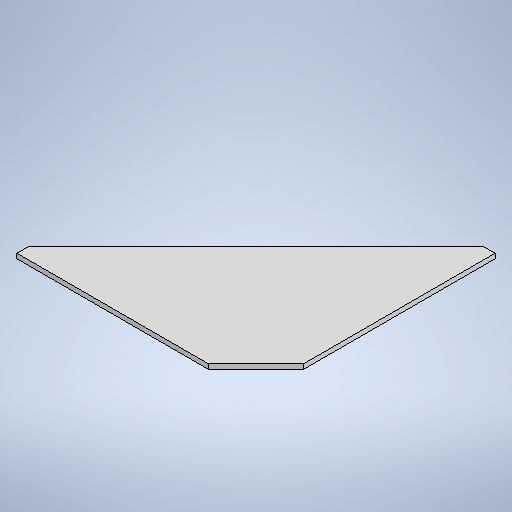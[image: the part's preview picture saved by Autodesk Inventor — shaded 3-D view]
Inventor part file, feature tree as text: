
AUTODESK INVENTOR PART (.ipt)
format: ipt  version: 2025 (Build 290162010, 162A)  size: 282,112 bytes
history: native  units: mm
features: other x2, sheet_metal_op x1, sketch x1
ambient origin geometry x8: Origin, YZ Plane, XZ Plane, XY Plane, X Axis, Y Axis, Z Axis, Center Point
bodies: Body1 (feature_tree)
feature tree (4):
  sheet_metal_op  "Face3"
  sketch  "Sketch1"  dims[d61=500.0mm d156=4.0mm d162=200.0mm d163=10.0mm d164=40.0mm d165=40.0mm]
  other  "Plate5"
  other  "Definition1"
